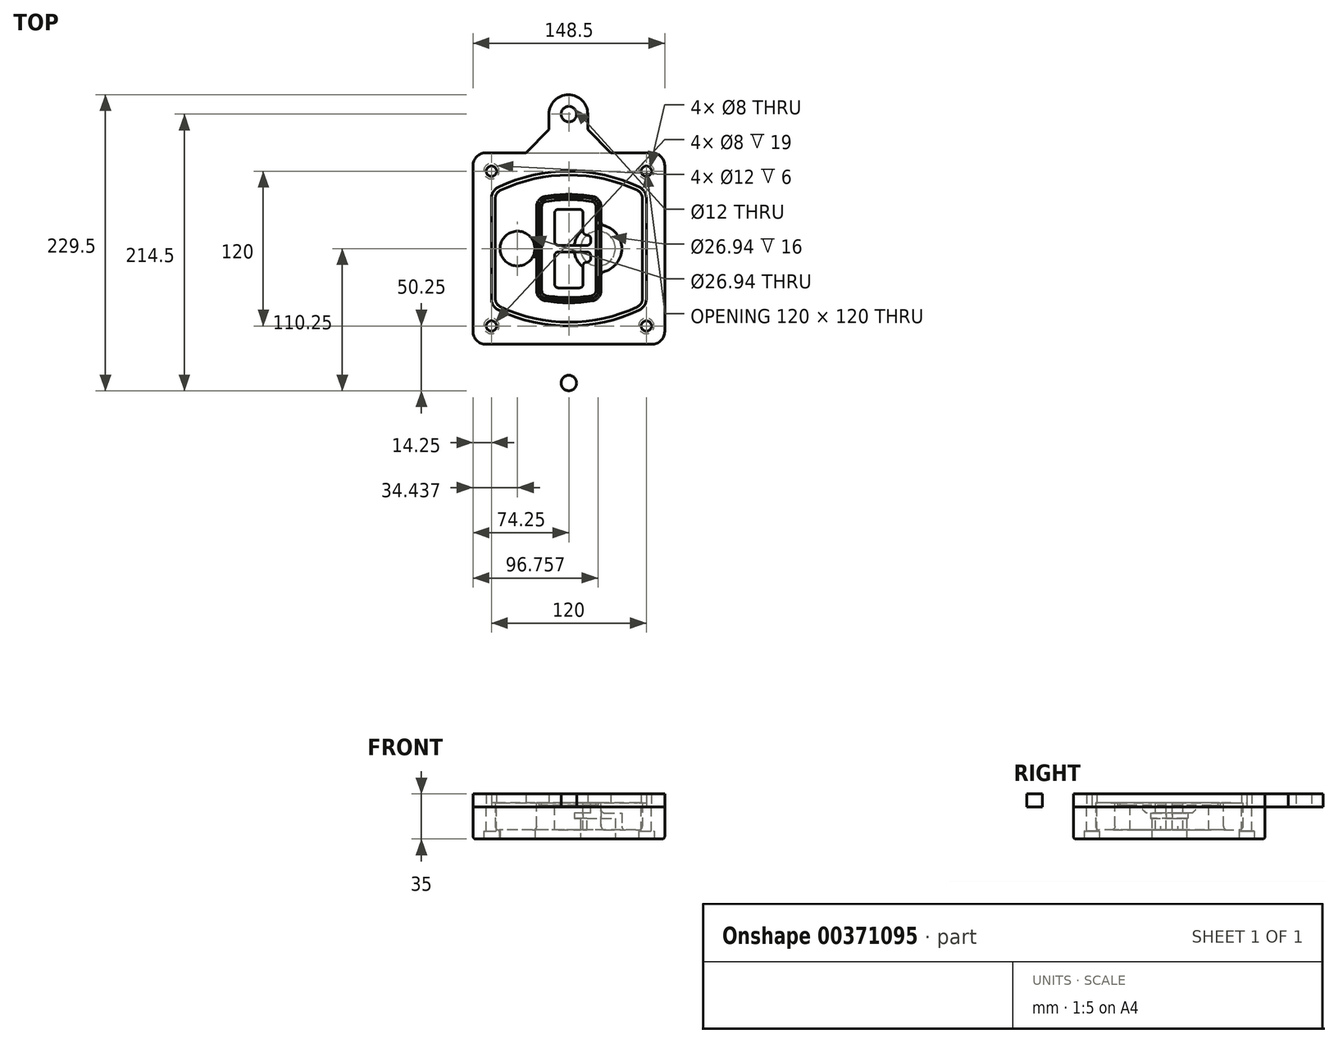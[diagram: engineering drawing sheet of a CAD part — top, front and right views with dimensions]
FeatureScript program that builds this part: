
annotation { "Feature Type Name" : "Feature", "Feature Type Description" : "" }
export const myFeature = defineFeature(function(context is Context, id is Id, definition is map)
    precondition{}
    {
        {
            var Q0;
            Q0=qCreatedBy(makeId("Top.planeOp"),FACE);
            var sketch = newSketch(context, id + "F0", { "sketchPlane" : qUnion([Q0])});
            skPoint(sketch, "E0.rect.middle", {"position": v(0, 0) * mm});
            skLineSegment(sketch, "E1.bottom", {"start": v(-64.25, -74.25) * mm, "end": v(64.25, -74.25) * mm});
            skLineSegment(sketch, "E1.top", {"start": v(-64.25, 74.25) * mm, "end": v(64.25, 74.25) * mm});
            skLineSegment(sketch, "E1.left", {"start": v(-74.25, -64.25) * mm, "end": v(-74.25, 64.25) * mm});
            skLineSegment(sketch, "E1.right", {"start": v(74.25, -64.25) * mm, "end": v(74.25, 64.25) * mm});
            skLineSegment(sketch, "E2", {"start": v(-74.25, 74.25) * mm, "end": v(74.25, -74.25) * mm, "construction": true});
            skLineSegment(sketch, "E3", {"start": v(74.25, 74.25) * mm, "end": v(-74.25, -74.25) * mm, "construction": true});
            skCircle(sketch, "E4", {"center": v(-60, 60) * mm, "radius": 4 * mm});
            skCircle(sketch, "E5", {"center": v(60, 60) * mm, "radius": 4 * mm});
            skCircle(sketch, "E6", {"center": v(60, -60) * mm, "radius": 4 * mm});
            skCircle(sketch, "E7", {"center": v(-60, -60) * mm, "radius": 4 * mm});
            skLineSegment(sketch, "E8", {"start": v(-60, 60) * mm, "end": v(60, 60) * mm, "construction": true});
            skLineSegment(sketch, "E9", {"start": v(60, 60) * mm, "end": v(60, -60) * mm, "construction": true});
            skLineSegment(sketch, "E10", {"start": v(60, -60) * mm, "end": v(-60, -60) * mm, "construction": true});
            skLineSegment(sketch, "E11", {"start": v(-60, -60) * mm, "end": v(-60, 60) * mm, "construction": true});
            skLineSegment(sketch, "E12", {"start": v(-60, 38.83) * mm, "end": v(-60, -38.83) * mm});
            skLineSegment(sketch, "E13", {"start": v(60, 38.83) * mm, "end": v(60, -38.83) * mm});
            skArc(sketch, "E14", {"start": v(54.26, 47.88) * mm, "mid": v(0, 60) * mm, "end": v(-54.26, 47.88) * mm});
            skArc(sketch, "E15", {"start": v(-54.26, -47.88) * mm, "mid": v(0, -60) * mm, "end": v(54.26, -47.88) * mm});
            skLineSegment(sketch, "E16", {"start": v(-60, 0) * mm, "end": v(60, 0) * mm, "construction": true});
            skPoint(sketch, "E17.visualSharp", {"position": v(-60, -45) * mm});
            skArc(sketch, "E17.filletArc", {"start": v(-60, -38.83) * mm, "mid": v(-58.44, -44.2) * mm, "end": v(-54.26, -47.88) * mm});
            skPoint(sketch, "E18.visualSharp", {"position": v(-60, 45) * mm});
            skArc(sketch, "E18.filletArc", {"start": v(-54.26, 47.88) * mm, "mid": v(-58.44, 44.2) * mm, "end": v(-60, 38.83) * mm});
            skPoint(sketch, "E19.visualSharp", {"position": v(60, 45) * mm});
            skArc(sketch, "E19.filletArc", {"start": v(60, 38.83) * mm, "mid": v(58.44, 44.2) * mm, "end": v(54.26, 47.88) * mm});
            skPoint(sketch, "E20.visualSharp", {"position": v(60, -45) * mm});
            skArc(sketch, "E20.filletArc", {"start": v(54.26, -47.88) * mm, "mid": v(58.44, -44.2) * mm, "end": v(60, -38.83) * mm});
            skPoint(sketch, "E21.visualSharp", {"position": v(-74.25, 74.25) * mm});
            skArc(sketch, "E21.filletArc", {"start": v(-64.25, 74.25) * mm, "mid": v(-71.32, 71.32) * mm, "end": v(-74.25, 64.25) * mm});
            skPoint(sketch, "E22.visualSharp", {"position": v(74.25, 74.25) * mm});
            skArc(sketch, "E22.filletArc", {"start": v(74.25, 64.25) * mm, "mid": v(71.32, 71.32) * mm, "end": v(64.25, 74.25) * mm});
            skPoint(sketch, "E23.visualSharp", {"position": v(74.25, -74.25) * mm});
            skArc(sketch, "E23.filletArc", {"start": v(64.25, -74.25) * mm, "mid": v(71.32, -71.32) * mm, "end": v(74.25, -64.25) * mm});
            skPoint(sketch, "E24.visualSharp", {"position": v(-74.25, -74.25) * mm});
            skArc(sketch, "E24.filletArc", {"start": v(-74.25, -64.25) * mm, "mid": v(-71.32, -71.32) * mm, "end": v(-64.25, -74.25) * mm});
            skArc(sketch, "E25.0", {"start": v(57, 38.83) * mm, "mid": v(55.9, 42.58) * mm, "end": v(52.98, 45.17) * mm});
            skLineSegment(sketch, "E25.1", {"start": v(57, 38.83) * mm, "end": v(57, -38.83) * mm});
            skArc(sketch, "E25.2", {"start": v(52.98, -45.17) * mm, "mid": v(55.9, -42.58) * mm, "end": v(57, -38.83) * mm});
            skArc(sketch, "E25.3", {"start": v(-52.98, -45.17) * mm, "mid": v(0, -57) * mm, "end": v(52.98, -45.17) * mm});
            skArc(sketch, "E25.4", {"start": v(-57, -38.83) * mm, "mid": v(-55.9, -42.58) * mm, "end": v(-52.98, -45.17) * mm});
            skArc(sketch, "E25.5", {"start": v(52.98, 45.17) * mm, "mid": v(0, 57) * mm, "end": v(-52.98, 45.17) * mm});
            skLineSegment(sketch, "E25.6", {"start": v(-57, 38.83) * mm, "end": v(-57, -38.83) * mm});
            skArc(sketch, "E25.7", {"start": v(-52.98, 45.17) * mm, "mid": v(-55.9, 42.58) * mm, "end": v(-57, 38.83) * mm});
            skArc(sketch, "E26.0", {"start": v(-55.96, 51.5) * mm, "mid": v(-61.82, 46.33) * mm, "end": v(-64, 38.83) * mm});
            skArc(sketch, "E26.1", {"start": v(55.96, 51.5) * mm, "mid": v(0, 64) * mm, "end": v(-55.96, 51.5) * mm});
            skArc(sketch, "E26.2", {"start": v(64, 38.83) * mm, "mid": v(61.82, 46.33) * mm, "end": v(55.96, 51.5) * mm});
            skLineSegment(sketch, "E26.3", {"start": v(64, 38.83) * mm, "end": v(64, -38.83) * mm});
            skArc(sketch, "E26.4", {"start": v(55.96, -51.5) * mm, "mid": v(61.82, -46.33) * mm, "end": v(64, -38.83) * mm});
            skLineSegment(sketch, "E26.5", {"start": v(-64, 38.83) * mm, "end": v(-64, -38.83) * mm});
            skArc(sketch, "E26.6", {"start": v(-55.96, -51.5) * mm, "mid": v(0, -64) * mm, "end": v(55.96, -51.5) * mm});
            skArc(sketch, "E26.7", {"start": v(-64, -38.83) * mm, "mid": v(-61.82, -46.33) * mm, "end": v(-55.96, -51.5) * mm});
            skSolve(sketch);
        }
        {
            var Q0;
            Q0=makeQuery(id+"F0.imprint","IMPRINT",FACE,{"disambiguationData":[TD([[makeQuery(id+"F0.imprint","IMPRINT",EDGE,{"derivedFrom":sQuery(id+"F0.wireOp",EDGE,"E1.bottom")}),1.0]])]});
            var Q1;
            Q1=makeQuery(id+"F0.imprint","IMPRINT",FACE,{"disambiguationData":[TD([[makeQuery(id+"F0.imprint","IMPRINT",EDGE,{"derivedFrom":sQuery(id+"F0.wireOp",EDGE,"E12")}),1.0]])]});
            var Q2;
            Q2=makeQuery(id+"F0.imprint","IMPRINT",FACE,{"disambiguationData":[TD([[makeQuery(id+"F0.imprint","IMPRINT",EDGE,{"derivedFrom":sQuery(id+"F0.wireOp",EDGE,"E25.0")}),1.0]])]});
            var Q3;
            Q3=makeQuery(id+"F0.imprint","IMPRINT",FACE,{"disambiguationData":[TD([[makeQuery(id+"F0.imprint","IMPRINT",EDGE,{"derivedFrom":sQuery(id+"F0.wireOp",EDGE,"E12")}),-1.0]])]});
            extrude(context, id + "F1", {"entities" : qUnion([Q0, Q1, Q2, Q3]), "oppositeDirection" : true, "depth" : 25 * mm});
        }
        {
            var Q0;
            Q0=makeQuery(id+"F0.imprint","IMPRINT",FACE,{"disambiguationData":[TD([[makeQuery(id+"F0.imprint","IMPRINT",EDGE,{"derivedFrom":sQuery(id+"F0.wireOp",EDGE,"E12")}),1.0]])]});
            extrude(context, id + "F2", {"entities" : qUnion([Q0]), "operationType" : NewBodyOperationType.ADD, "depth" : 3 * mm});
        }
        {
            var Q0;
            Q0=makeQuery(id+"F0.imprint","IMPRINT",FACE,{"disambiguationData":[TD([[makeQuery(id+"F0.imprint","IMPRINT",EDGE,{"derivedFrom":sQuery(id+"F0.wireOp",EDGE,"E25.0")}),1.0]])]});
            extrude(context, id + "F3", {"entities" : qUnion([Q0]), "operationType" : NewBodyOperationType.REMOVE, "oppositeDirection" : true, "depth" : 18 * mm});
        }
        {
            var Q0;
            Q0=makeQuery(id+"F2.opExtrude","CAP_FACE",FACE,{"disambiguationData":[OSD([sQuery(id+"F0.wireOp",EDGE,"E12"),sQuery(id+"F0.wireOp",EDGE,"E13"),sQuery(id+"F0.wireOp",EDGE,"E14"),sQuery(id+"F0.wireOp",EDGE,"E15"),sQuery(id+"F0.wireOp",EDGE,"E17.filletArc"),sQuery(id+"F0.wireOp",EDGE,"E18.filletArc"),sQuery(id+"F0.wireOp",EDGE,"E19.filletArc"),sQuery(id+"F0.wireOp",EDGE,"E20.filletArc"),sQuery(id+"F0.wireOp",EDGE,"E25.0"),sQuery(id+"F0.wireOp",EDGE,"E25.1"),sQuery(id+"F0.wireOp",EDGE,"E25.2"),sQuery(id+"F0.wireOp",EDGE,"E25.3"),sQuery(id+"F0.wireOp",EDGE,"E25.4"),sQuery(id+"F0.wireOp",EDGE,"E25.5"),sQuery(id+"F0.wireOp",EDGE,"E25.6"),sQuery(id+"F0.wireOp",EDGE,"E25.7")])],"isStart":false});
            var sketch = newSketch(context, id + "F4", { "sketchPlane" : qUnion([Q0])});
            skArc(sketch, "E27.0", {"start": v(-18.34, -40.45) * mm, "mid": v(0, -42) * mm, "end": v(18.34, -40.45) * mm});
            skArc(sketch, "E28.0", {"start": v(18.34, 40.45) * mm, "mid": v(0, 42) * mm, "end": v(-18.34, 40.45) * mm});
            skLineSegment(sketch, "E29", {"start": v(-25, 32.57) * mm, "end": v(-25, -32.57) * mm});
            skLineSegment(sketch, "E30", {"start": v(25, 32.57) * mm, "end": v(25, -32.57) * mm});
            skLineSegment(sketch, "E31", {"start": v(-25, 39.1) * mm, "end": v(25, 39.1) * mm, "construction": true});
            skLineSegment(sketch, "E32", {"start": v(-25, -39.1) * mm, "end": v(25, -39.1) * mm, "construction": true});
            skPoint(sketch, "E33.visualSharp", {"position": v(-25, 39.1) * mm});
            skArc(sketch, "E33.filletArc", {"start": v(-18.34, 40.45) * mm, "mid": v(-23.11, 37.73) * mm, "end": v(-25, 32.57) * mm});
            skPoint(sketch, "E34.visualSharp", {"position": v(25, 39.1) * mm});
            skArc(sketch, "E34.filletArc", {"start": v(25, 32.57) * mm, "mid": v(23.11, 37.73) * mm, "end": v(18.34, 40.45) * mm});
            skPoint(sketch, "E35.visualSharp", {"position": v(25, -39.1) * mm});
            skArc(sketch, "E35.filletArc", {"start": v(18.34, -40.45) * mm, "mid": v(23.11, -37.73) * mm, "end": v(25, -32.57) * mm});
            skPoint(sketch, "E36.visualSharp", {"position": v(-25, -39.1) * mm});
            skArc(sketch, "E36.filletArc", {"start": v(-25, -32.57) * mm, "mid": v(-23.11, -37.73) * mm, "end": v(-18.34, -40.45) * mm});
            skArc(sketch, "E37.0", {"start": v(52.98, 45.17) * mm, "mid": v(0, 57) * mm, "end": v(-52.98, 45.17) * mm});
            skArc(sketch, "E37.1", {"start": v(-52.98, 45.17) * mm, "mid": v(-55.9, 42.58) * mm, "end": v(-57, 38.83) * mm});
            skLineSegment(sketch, "E37.2", {"start": v(-57, 38.83) * mm, "end": v(-57, -38.83) * mm});
            skArc(sketch, "E37.3", {"start": v(-57, -38.83) * mm, "mid": v(-55.9, -42.58) * mm, "end": v(-52.98, -45.17) * mm});
            skArc(sketch, "E37.4", {"start": v(-52.98, -45.17) * mm, "mid": v(0, -57) * mm, "end": v(52.98, -45.17) * mm});
            skArc(sketch, "E37.5", {"start": v(52.98, -45.17) * mm, "mid": v(55.9, -42.58) * mm, "end": v(57, -38.83) * mm});
            skLineSegment(sketch, "E37.6", {"start": v(57, 38.83) * mm, "end": v(57, -38.83) * mm});
            skArc(sketch, "E37.7", {"start": v(57, 38.83) * mm, "mid": v(55.9, 42.58) * mm, "end": v(52.98, 45.17) * mm});
            skLineSegment(sketch, "E38.0", {"start": v(23, 32.57) * mm, "end": v(23, -32.57) * mm});
            skArc(sketch, "E38.1", {"start": v(18, -38.48) * mm, "mid": v(21.58, -36.44) * mm, "end": v(23, -32.57) * mm});
            skArc(sketch, "E38.2", {"start": v(-18, -38.48) * mm, "mid": v(0, -40) * mm, "end": v(18, -38.48) * mm});
            skArc(sketch, "E38.3", {"start": v(-23, -32.57) * mm, "mid": v(-21.58, -36.44) * mm, "end": v(-18, -38.48) * mm});
            skLineSegment(sketch, "E38.4", {"start": v(-23, 32.57) * mm, "end": v(-23, -32.57) * mm});
            skArc(sketch, "E38.5", {"start": v(23, 32.57) * mm, "mid": v(21.58, 36.44) * mm, "end": v(18, 38.48) * mm});
            skArc(sketch, "E38.6", {"start": v(-18, 38.48) * mm, "mid": v(-21.58, 36.44) * mm, "end": v(-23, 32.57) * mm});
            skArc(sketch, "E38.7", {"start": v(18, 38.48) * mm, "mid": v(0, 40) * mm, "end": v(-18, 38.48) * mm});
            skArc(sketch, "E39.0", {"start": v(21, 32.57) * mm, "mid": v(20.06, 35.15) * mm, "end": v(17.67, 36.5) * mm});
            skLineSegment(sketch, "E39.1", {"start": v(21, 32.57) * mm, "end": v(21, -32.57) * mm});
            skArc(sketch, "E39.2", {"start": v(17.67, -36.5) * mm, "mid": v(20.06, -35.15) * mm, "end": v(21, -32.57) * mm});
            skArc(sketch, "E39.3", {"start": v(-17.67, -36.5) * mm, "mid": v(0, -38) * mm, "end": v(17.67, -36.5) * mm});
            skArc(sketch, "E39.4", {"start": v(-21, -32.57) * mm, "mid": v(-20.06, -35.15) * mm, "end": v(-17.67, -36.5) * mm});
            skArc(sketch, "E39.5", {"start": v(17.67, 36.5) * mm, "mid": v(0, 38) * mm, "end": v(-17.67, 36.5) * mm});
            skLineSegment(sketch, "E39.6", {"start": v(-21, 32.57) * mm, "end": v(-21, -32.57) * mm});
            skArc(sketch, "E39.7", {"start": v(-17.67, 36.5) * mm, "mid": v(-20.06, 35.15) * mm, "end": v(-21, 32.57) * mm});
            skLineSegment(sketch, "E40", {"start": v(-25, 0) * mm, "end": v(25, 0) * mm, "construction": true});
            skLineSegment(sketch, "E41", {"start": v(-11, 5.5) * mm, "end": v(-11, 27.5) * mm});
            skLineSegment(sketch, "E42", {"start": v(-8, 30.5) * mm, "end": v(8, 30.5) * mm});
            skLineSegment(sketch, "E43", {"start": v(11, 27.5) * mm, "end": v(11, 13.5) * mm});
            skLineSegment(sketch, "E44", {"start": v(14, 10.5) * mm, "end": v(14, 10.5) * mm});
            skLineSegment(sketch, "E45", {"start": v(17, 7.5) * mm, "end": v(17, 5.5) * mm});
            skLineSegment(sketch, "E46", {"start": v(14, 2.5) * mm, "end": v(-8, 2.5) * mm});
            skPoint(sketch, "E47.visualSharp", {"position": v(-11, 30.5) * mm});
            skArc(sketch, "E47.filletArc", {"start": v(-8, 30.5) * mm, "mid": v(-10.12, 29.62) * mm, "end": v(-11, 27.5) * mm});
            skPoint(sketch, "E48.visualSharp", {"position": v(11, 30.5) * mm});
            skArc(sketch, "E48.filletArc", {"start": v(11, 27.5) * mm, "mid": v(10.12, 29.62) * mm, "end": v(8, 30.5) * mm});
            skPoint(sketch, "E49.visualSharp", {"position": v(11, 10.5) * mm});
            skArc(sketch, "E49.filletArc", {"start": v(11, 13.5) * mm, "mid": v(11.88, 11.38) * mm, "end": v(14, 10.5) * mm});
            skPoint(sketch, "E50.visualSharp", {"position": v(17, 10.5) * mm});
            skArc(sketch, "E50.filletArc", {"start": v(17, 7.5) * mm, "mid": v(16.12, 9.62) * mm, "end": v(14, 10.5) * mm});
            skPoint(sketch, "E51.visualSharp", {"position": v(17, 2.5) * mm});
            skArc(sketch, "E51.filletArc", {"start": v(14, 2.5) * mm, "mid": v(16.12, 3.38) * mm, "end": v(17, 5.5) * mm});
            skPoint(sketch, "E52.visualSharp", {"position": v(-11, 2.5) * mm});
            skArc(sketch, "E52.filletArc", {"start": v(-11, 5.5) * mm, "mid": v(-10.12, 3.38) * mm, "end": v(-8, 2.5) * mm});
            skLineSegment(sketch, "E53.0.MirrorCS", {"start": v(14, -2.5) * mm, "end": v(-8, -2.5) * mm});
            skArc(sketch, "E54.0.MirrorCS", {"start": v(-11, -5.5) * mm, "mid": v(-10.12, -3.38) * mm, "end": v(-8, -2.5) * mm});
            skLineSegment(sketch, "E55.0.MirrorCS", {"start": v(-11, -5.5) * mm, "end": v(-11, -27.5) * mm});
            skArc(sketch, "E56.0.MirrorCS", {"start": v(-8, -30.5) * mm, "mid": v(-10.12, -29.62) * mm, "end": v(-11, -27.5) * mm});
            skLineSegment(sketch, "E57.0.MirrorCS", {"start": v(-8, -30.5) * mm, "end": v(8, -30.5) * mm});
            skArc(sketch, "E58.0.MirrorCS", {"start": v(11, -27.5) * mm, "mid": v(10.12, -29.62) * mm, "end": v(8, -30.5) * mm});
            skLineSegment(sketch, "E59.0.MirrorCS", {"start": v(11, -27.5) * mm, "end": v(11, -13.5) * mm});
            skArc(sketch, "E60.0.MirrorCS", {"start": v(11, -13.5) * mm, "mid": v(11.88, -11.38) * mm, "end": v(14, -10.5) * mm});
            skArc(sketch, "E61.0.MirrorCS", {"start": v(17, -7.5) * mm, "mid": v(16.12, -9.62) * mm, "end": v(14, -10.5) * mm});
            skLineSegment(sketch, "E62.0.MirrorCS", {"start": v(17, -7.5) * mm, "end": v(17, -5.5) * mm});
            skArc(sketch, "E63.0.MirrorCS", {"start": v(14, -2.5) * mm, "mid": v(16.12, -3.38) * mm, "end": v(17, -5.5) * mm});
            skSolve(sketch);
        }
        {
            var Q0;
            Q0=makeQuery(id+"F4.imprint","IMPRINT",FACE,{"disambiguationData":[TD([[makeQuery(id+"F4.imprint","IMPRINT",EDGE,{"derivedFrom":sQuery(id+"F4.wireOp",EDGE,"E27.0")}),1.0]])]});
            var Q1;
            Q1=makeQuery(id+"F4.imprint","IMPRINT",FACE,{"disambiguationData":[TD([[makeQuery(id+"F4.imprint","IMPRINT",EDGE,{"derivedFrom":sQuery(id+"F4.wireOp",EDGE,"E38.0")}),-1.0]])]});
            var Q2;
            Q2=makeQuery(id+"F4.imprint","IMPRINT",FACE,{"disambiguationData":[TD([[makeQuery(id+"F4.imprint","IMPRINT",EDGE,{"derivedFrom":sQuery(id+"F4.wireOp",EDGE,"E39.0")}),1.0]])]});
            extrude(context, id + "F5", {"entities" : qUnion([Q0, Q1, Q2]), "operationType" : NewBodyOperationType.ADD, "endBound" : BoundingType.UP_TO_NEXT, "oppositeDirection" : true, "depth" : 25 * mm});
        }
        {
            var Q0;
            Q0=makeQuery(id+"F4.imprint","IMPRINT",FACE,{"disambiguationData":[TD([[makeQuery(id+"F4.imprint","IMPRINT",EDGE,{"derivedFrom":sQuery(id+"F4.wireOp",EDGE,"E38.0")}),-1.0]])]});
            extrude(context, id + "F6", {"entities" : qUnion([Q0]), "operationType" : NewBodyOperationType.REMOVE, "oppositeDirection" : true, "depth" : 2 * mm});
        }
        {
            var Q0;
            Q0=makeQuery(id+"F1.opExtrude","CAP_FACE",FACE,{"disambiguationData":[OSD([sQuery(id+"F0.wireOp",EDGE,"E1.bottom"),sQuery(id+"F0.wireOp",EDGE,"E1.top"),sQuery(id+"F0.wireOp",EDGE,"E1.left"),sQuery(id+"F0.wireOp",EDGE,"E1.right"),sQuery(id+"F0.wireOp",EDGE,"E4"),sQuery(id+"F0.wireOp",EDGE,"E5"),sQuery(id+"F0.wireOp",EDGE,"E6"),sQuery(id+"F0.wireOp",EDGE,"E7"),sQuery(id+"F0.wireOp",EDGE,"E21.filletArc"),sQuery(id+"F0.wireOp",EDGE,"E22.filletArc"),sQuery(id+"F0.wireOp",EDGE,"E23.filletArc"),sQuery(id+"F0.wireOp",EDGE,"E24.filletArc")])],"isStart":false});
            var sketch = newSketch(context, id + "F7", { "sketchPlane" : qUnion([Q0])});
            skCircle(sketch, "E64", {"center": v(22.5, 0) * mm, "radius": 13.47 * mm});
            skCircle(sketch, "E65", {"center": v(-39.81, 0) * mm, "radius": 13.47 * mm});
            skLineSegment(sketch, "E66", {"start": v(74.25, 0) * mm, "end": v(-74.25, 0) * mm});
            skCircle(sketch, "E67", {"center": v(22.5, 0) * mm, "radius": 18.47 * mm});
            skCircle(sketch, "E68", {"center": v(60, -60) * mm, "radius": 6 * mm});
            skCircle(sketch, "E69", {"center": v(-60, -60) * mm, "radius": 6 * mm});
            skCircle(sketch, "E70", {"center": v(-60, 60) * mm, "radius": 6 * mm});
            skCircle(sketch, "E71", {"center": v(60, 60) * mm, "radius": 6 * mm});
            skSolve(sketch);
        }
        {
            var Q0;
            {var subQ1=sQuery(id+"F7.wireOp",EDGE,"E66");var subQ4=sQuery(id+"F7.wireOp",EDGE,"E64");var subQ6=makeQuery(id+"F7.imprint","INTERSECT",VERTEX,{"disambiguationData":[OD(0.0)],"derivedFrom":[subQ4,subQ1]});Q0=makeQuery(id+"F7.imprint","IMPRINT",FACE,{"disambiguationData":[TD([[makeQuery(id+"F7.imprint","IMPRINT",EDGE,{"disambiguationData":[TD([[subQ6,-1.0]])],"derivedFrom":subQ4}),-1.0]])]});}
            var Q1;
            {var subQ0=sQuery(id+"F7.wireOp",EDGE,"E66");var subQ1=sQuery(id+"F7.wireOp",EDGE,"E64");var subQ3=makeQuery(id+"F7.imprint","INTERSECT",VERTEX,{"disambiguationData":[OD(0.0)],"derivedFrom":[subQ1,subQ0]});Q1=makeQuery(id+"F7.imprint","IMPRINT",FACE,{"disambiguationData":[TD([[makeQuery(id+"F7.imprint","IMPRINT",EDGE,{"disambiguationData":[TD([[subQ3,-1.0]])],"derivedFrom":subQ1}),1.0]])]});}
            var Q2;
            {var subQ0=sQuery(id+"F7.wireOp",EDGE,"E66");var subQ1=sQuery(id+"F7.wireOp",EDGE,"E64");var subQ3=makeQuery(id+"F7.imprint","INTERSECT",VERTEX,{"disambiguationData":[OD(0.0)],"derivedFrom":[subQ1,subQ0]});Q2=makeQuery(id+"F7.imprint","IMPRINT",FACE,{"disambiguationData":[TD([[makeQuery(id+"F7.imprint","IMPRINT",EDGE,{"disambiguationData":[TD([[subQ3,1.0]])],"derivedFrom":subQ1}),1.0]])]});}
            var Q3;
            {var subQ1=sQuery(id+"F7.wireOp",EDGE,"E66");var subQ4=sQuery(id+"F7.wireOp",EDGE,"E64");var subQ6=makeQuery(id+"F7.imprint","INTERSECT",VERTEX,{"disambiguationData":[OD(0.0)],"derivedFrom":[subQ4,subQ1]});Q3=makeQuery(id+"F7.imprint","IMPRINT",FACE,{"disambiguationData":[TD([[makeQuery(id+"F7.imprint","IMPRINT",EDGE,{"disambiguationData":[TD([[subQ6,1.0]])],"derivedFrom":subQ4}),-1.0]])]});}
            extrude(context, id + "F8", {"entities" : qUnion([Q0, Q1, Q2, Q3]), "operationType" : NewBodyOperationType.ADD, "oppositeDirection" : true, "depth" : 20 * mm});
        }
        {
            var Q0;
            {var subQ0=sQuery(id+"F7.wireOp",EDGE,"E66");var subQ1=sQuery(id+"F7.wireOp",EDGE,"E64");var subQ3=makeQuery(id+"F7.imprint","INTERSECT",VERTEX,{"disambiguationData":[OD(0.0)],"derivedFrom":[subQ1,subQ0]});Q0=makeQuery(id+"F7.imprint","IMPRINT",FACE,{"disambiguationData":[TD([[makeQuery(id+"F7.imprint","IMPRINT",EDGE,{"disambiguationData":[TD([[subQ3,-1.0]])],"derivedFrom":subQ1}),1.0]])]});}
            var Q1;
            {var subQ0=sQuery(id+"F7.wireOp",EDGE,"E66");var subQ1=sQuery(id+"F7.wireOp",EDGE,"E64");var subQ3=makeQuery(id+"F7.imprint","INTERSECT",VERTEX,{"disambiguationData":[OD(0.0)],"derivedFrom":[subQ1,subQ0]});Q1=makeQuery(id+"F7.imprint","IMPRINT",FACE,{"disambiguationData":[TD([[makeQuery(id+"F7.imprint","IMPRINT",EDGE,{"disambiguationData":[TD([[subQ3,1.0]])],"derivedFrom":subQ1}),1.0]])]});}
            extrude(context, id + "F9", {"entities" : qUnion([Q0, Q1]), "operationType" : NewBodyOperationType.REMOVE, "oppositeDirection" : true, "depth" : 16 * mm});
        }
        {
            var Q0;
            {var subQ0=sQuery(id+"F7.wireOp",EDGE,"E66");var subQ1=sQuery(id+"F7.wireOp",EDGE,"E65");var subQ3=makeQuery(id+"F7.imprint","INTERSECT",VERTEX,{"disambiguationData":[OD(0.0)],"derivedFrom":[subQ1,subQ0]});Q0=makeQuery(id+"F7.imprint","IMPRINT",FACE,{"disambiguationData":[TD([[makeQuery(id+"F7.imprint","IMPRINT",EDGE,{"disambiguationData":[TD([[subQ3,-1.0]])],"derivedFrom":subQ1}),1.0]])]});}
            var Q1;
            {var subQ0=sQuery(id+"F7.wireOp",EDGE,"E66");var subQ1=sQuery(id+"F7.wireOp",EDGE,"E65");var subQ3=makeQuery(id+"F7.imprint","INTERSECT",VERTEX,{"disambiguationData":[OD(0.0)],"derivedFrom":[subQ1,subQ0]});Q1=makeQuery(id+"F7.imprint","IMPRINT",FACE,{"disambiguationData":[TD([[makeQuery(id+"F7.imprint","IMPRINT",EDGE,{"disambiguationData":[TD([[subQ3,1.0]])],"derivedFrom":subQ1}),1.0]])]});}
            extrude(context, id + "F10", {"entities" : qUnion([Q0, Q1]), "operationType" : NewBodyOperationType.REMOVE, "oppositeDirection" : true, "depth" : 25 * mm});
        }
        {
            var Q0;
            Q0=makeQuery(id+"F7.imprint","IMPRINT",FACE,{"disambiguationData":[TD([[makeQuery(id+"F7.imprint","IMPRINT",EDGE,{"derivedFrom":sQuery(id+"F7.wireOp",EDGE,"E68")}),1.0]])]});
            var Q1;
            Q1=makeQuery(id+"F7.imprint","IMPRINT",FACE,{"disambiguationData":[TD([[makeQuery(id+"F7.imprint","IMPRINT",EDGE,{"derivedFrom":makeQuery(id+"F1.opExtrude","CAP_EDGE",EDGE,{"disambiguationData":[OSD([sQuery(id+"F0.wireOp",EDGE,"E5")])],"isStart":false})}),-1.0]])]});
            var Q2;
            Q2=makeQuery(id+"F7.imprint","IMPRINT",FACE,{"disambiguationData":[TD([[makeQuery(id+"F7.imprint","IMPRINT",EDGE,{"derivedFrom":sQuery(id+"F7.wireOp",EDGE,"E69")}),1.0]])]});
            var Q3;
            Q3=makeQuery(id+"F7.imprint","IMPRINT",FACE,{"disambiguationData":[TD([[makeQuery(id+"F7.imprint","IMPRINT",EDGE,{"derivedFrom":makeQuery(id+"F1.opExtrude","CAP_EDGE",EDGE,{"disambiguationData":[OSD([sQuery(id+"F0.wireOp",EDGE,"E4")])],"isStart":false})}),-1.0]])]});
            var Q4;
            Q4=makeQuery(id+"F7.imprint","IMPRINT",FACE,{"disambiguationData":[TD([[makeQuery(id+"F7.imprint","IMPRINT",EDGE,{"derivedFrom":sQuery(id+"F7.wireOp",EDGE,"E70")}),1.0]])]});
            var Q5;
            Q5=makeQuery(id+"F7.imprint","IMPRINT",FACE,{"disambiguationData":[TD([[makeQuery(id+"F7.imprint","IMPRINT",EDGE,{"derivedFrom":makeQuery(id+"F1.opExtrude","CAP_EDGE",EDGE,{"disambiguationData":[OSD([sQuery(id+"F0.wireOp",EDGE,"E7")])],"isStart":false})}),-1.0]])]});
            var Q6;
            Q6=makeQuery(id+"F7.imprint","IMPRINT",FACE,{"disambiguationData":[TD([[makeQuery(id+"F7.imprint","IMPRINT",EDGE,{"derivedFrom":sQuery(id+"F7.wireOp",EDGE,"E71")}),1.0]])]});
            var Q7;
            Q7=makeQuery(id+"F7.imprint","IMPRINT",FACE,{"disambiguationData":[TD([[makeQuery(id+"F7.imprint","IMPRINT",EDGE,{"derivedFrom":makeQuery(id+"F1.opExtrude","CAP_EDGE",EDGE,{"disambiguationData":[OSD([sQuery(id+"F0.wireOp",EDGE,"E6")])],"isStart":false})}),-1.0]])]});
            extrude(context, id + "F11", {"entities" : qUnion([Q0, Q1, Q2, Q3, Q4, Q5, Q6, Q7]), "operationType" : NewBodyOperationType.REMOVE, "oppositeDirection" : true, "depth" : 6 * mm});
        }
        {
            var Q0;
            Q0=makeQuery(id+"F9.boolean.opBoolean","COPY",FACE,{"derivedFrom":makeQuery(id+"F9.opExtrude","CAP_FACE",FACE,{"disambiguationData":[OSD([sQuery(id+"F7.wireOp",EDGE,"E64")])],"isStart":false})});
            var sketch = newSketch(context, id + "F12", { "sketchPlane" : qUnion([Q0])});
            skArc(sketch, "E72.0", {"start": v(11, 14.45) * mm, "mid": v(6.45, 9.13) * mm, "end": v(4.2, 2.5) * mm});
            skArc(sketch, "E72.1", {"start": v(4.2, -2.5) * mm, "mid": v(6.45, -9.13) * mm, "end": v(11, -14.45) * mm});
            skLineSegment(sketch, "E73", {"start": v(4.2, -2.5) * mm, "end": v(14, -2.5) * mm});
            skLineSegment(sketch, "E74.0", {"start": v(14, 2.5) * mm, "end": v(4.2, 2.5) * mm});
            skArc(sketch, "E74.1", {"start": v(14, 2.5) * mm, "mid": v(16.12, 3.38) * mm, "end": v(17, 5.5) * mm});
            skLineSegment(sketch, "E74.2", {"start": v(17, 7.5) * mm, "end": v(17, 5.5) * mm});
            skArc(sketch, "E74.3", {"start": v(17, 7.5) * mm, "mid": v(16.12, 9.62) * mm, "end": v(14, 10.5) * mm});
            skArc(sketch, "E74.4", {"start": v(11, 13.5) * mm, "mid": v(11.88, 11.38) * mm, "end": v(14, 10.5) * mm});
            skLineSegment(sketch, "E74.5", {"start": v(11, 14.45) * mm, "end": v(11, 13.5) * mm});
            skLineSegment(sketch, "E74.7", {"start": v(14, -2.5) * mm, "end": v(4.2, -2.5) * mm});
            skArc(sketch, "E74.8", {"start": v(14, -2.5) * mm, "mid": v(16.12, -3.38) * mm, "end": v(17, -5.5) * mm});
            skLineSegment(sketch, "E74.9", {"start": v(17, -7.5) * mm, "end": v(17, -5.5) * mm});
            skArc(sketch, "E74.10", {"start": v(17, -7.5) * mm, "mid": v(16.12, -9.62) * mm, "end": v(14, -10.5) * mm});
            skArc(sketch, "E74.11", {"start": v(11, -13.5) * mm, "mid": v(11.88, -11.38) * mm, "end": v(14, -10.5) * mm});
            skLineSegment(sketch, "E74.12", {"start": v(11, -14.45) * mm, "end": v(11, -13.5) * mm});
            skPoint(sketch, "E75.orphan", {"position": v(11, -27.5) * mm});
            skPoint(sketch, "E76.orphan", {"position": v(-8, -2.5) * mm});
            skPoint(sketch, "E77.orphan", {"position": v(-8, 2.5) * mm});
            skPoint(sketch, "E78.orphan", {"position": v(11, 27.5) * mm});
            skSolve(sketch);
        }
        {
            var Q0;
            {var subQ7=sQuery(id+"F12.wireOp",EDGE,"E72.0");var subQ14=sQuery(id+"F12.wireOp",EDGE,"E72.1");var subQ16=sQuery(id+"F12.wireOp",EDGE,"E74.1");var subQ18=sQuery(id+"F12.wireOp",EDGE,"E74.8");Q0=qUnion([makeQuery(id+"F12.imprint","IMPRINT",FACE,{"disambiguationData":[TD([[makeQuery(id+"F12.imprint","IMPRINT",EDGE,{"derivedFrom":subQ7}),1.0]])]}),makeQuery(id+"F12.imprint","IMPRINT",FACE,{"disambiguationData":[TD([[makeQuery(id+"F12.imprint","IMPRINT",EDGE,{"derivedFrom":subQ14}),1.0]])]}),makeQuery(id+"F12.imprint","IMPRINT",FACE,{"disambiguationData":[TD([[makeQuery(id+"F12.imprint","IMPRINT",EDGE,{"derivedFrom":subQ16}),1.0]])]}),makeQuery(id+"F12.imprint","IMPRINT",FACE,{"disambiguationData":[TD([[makeQuery(id+"F12.imprint","IMPRINT",EDGE,{"derivedFrom":subQ18}),-1.0]])]})]);}
            var Q1;
            Q1=makeQuery(id+"F5.boolean.opBoolean","SPLIT",FACE,{"disambiguationData":[TD([makeQuery(id+"F5.opExtrude","SWEPT_FACE",FACE,{"disambiguationData":[OSD([sQuery(id+"F4.wireOp",EDGE,"E41")])]})])],"derivedFrom":makeQuery(id+"F3.boolean.opBoolean","COPY",FACE,{"derivedFrom":makeQuery(id+"F3.opExtrude","CAP_FACE",FACE,{"disambiguationData":[OSD([sQuery(id+"F0.wireOp",EDGE,"E25.0"),sQuery(id+"F0.wireOp",EDGE,"E25.1"),sQuery(id+"F0.wireOp",EDGE,"E25.2"),sQuery(id+"F0.wireOp",EDGE,"E25.3"),sQuery(id+"F0.wireOp",EDGE,"E25.4"),sQuery(id+"F0.wireOp",EDGE,"E25.5"),sQuery(id+"F0.wireOp",EDGE,"E25.6"),sQuery(id+"F0.wireOp",EDGE,"E25.7")])],"isStart":false})})});
            extrude(context, id + "F13", {"entities" : qUnion([Q0]), "operationType" : NewBodyOperationType.REMOVE, "endBound" : BoundingType.UP_TO_SURFACE, "endBoundEntityFace" : qUnion([Q1]), "depth" : 25 * mm});
        }
        {
            var Q0;
            Q0=makeQuery(id+"F3.boolean.opBoolean","COPY",EDGE,{"derivedFrom":makeQuery(id+"F3.opExtrude","CAP_EDGE",EDGE,{"disambiguationData":[OSD([sQuery(id+"F0.wireOp",EDGE,"E25.6")])],"isStart":false})});
            var Q1;
            Q1=makeQuery(id+"F8.boolean.opBoolean","INTERSECT",EDGE,{"derivedFrom":[makeQuery(id+"F5.opExtrude","SWEPT_FACE",FACE,{"disambiguationData":[OSD([sQuery(id+"F4.wireOp",EDGE,"E30")])]}),makeQuery(id+"F8.opExtrude","CAP_FACE",FACE,{"disambiguationData":[OSD([sQuery(id+"F7.wireOp",EDGE,"E67")])],"isStart":false})]});
            var Q2;
            Q2=makeQuery(id+"F8.boolean.opBoolean","INTERSECT",EDGE,{"disambiguationData":[OD(1.0)],"derivedFrom":[makeQuery(id+"F5.opExtrude","SWEPT_FACE",FACE,{"disambiguationData":[OSD([sQuery(id+"F4.wireOp",EDGE,"E30")])]}),makeQuery(id+"F8.opExtrude","SWEPT_FACE",FACE,{"disambiguationData":[OSD([sQuery(id+"F7.wireOp",EDGE,"E67")])]})]});
            var Q3;
            {var subQ0=sQuery(id+"F4.wireOp",EDGE,"E30");Q3=makeQuery(id+"F8.boolean.opBoolean","SPLIT",EDGE,{"disambiguationData":[TD([makeQuery(id+"F5.opExtrude","SWEPT_FACE",FACE,{"disambiguationData":[OSD([sQuery(id+"F4.wireOp",EDGE,"E35.filletArc")])]})])],"derivedFrom":makeQuery(id+"F5.opExtrude","CAP_EDGE",EDGE,{"disambiguationData":[OSD([subQ0])],"isStart":false})});}
            var Q4;
            {var subQ0=sQuery(id+"F0.wireOp",EDGE,"E25.7");var subQ1=sQuery(id+"F0.wireOp",EDGE,"E25.1");var subQ2=sQuery(id+"F0.wireOp",EDGE,"E25.6");var subQ3=sQuery(id+"F0.wireOp",EDGE,"E25.5");var subQ4=sQuery(id+"F0.wireOp",EDGE,"E25.4");var subQ5=sQuery(id+"F0.wireOp",EDGE,"E25.0");var subQ6=sQuery(id+"F0.wireOp",EDGE,"E25.2");var subQ7=sQuery(id+"F0.wireOp",EDGE,"E25.3");Q4=makeQuery(id+"F8.boolean.opBoolean","INTERSECT",EDGE,{"derivedFrom":[makeQuery(id+"F5.boolean.opBoolean","SPLIT",FACE,{"disambiguationData":[TD([makeQuery(id+"F2.opExtrude","SWEPT_FACE",FACE,{"disambiguationData":[OSD([subQ5])]})])],"derivedFrom":makeQuery(id+"F3.boolean.opBoolean","COPY",FACE,{"derivedFrom":makeQuery(id+"F3.opExtrude","CAP_FACE",FACE,{"disambiguationData":[OSD([subQ5,subQ1,subQ6,subQ7,subQ4,subQ3,subQ2,subQ0])],"isStart":false})})}),makeQuery(id+"F8.opExtrude","SWEPT_FACE",FACE,{"disambiguationData":[OSD([sQuery(id+"F7.wireOp",EDGE,"E67")])]})]});}
            var Q5;
            Q5=makeQuery(id+"F8.boolean.opBoolean","INTERSECT",EDGE,{"disambiguationData":[OD(0.0)],"derivedFrom":[makeQuery(id+"F5.opExtrude","SWEPT_FACE",FACE,{"disambiguationData":[OSD([sQuery(id+"F4.wireOp",EDGE,"E30")])]}),makeQuery(id+"F8.opExtrude","SWEPT_FACE",FACE,{"disambiguationData":[OSD([sQuery(id+"F7.wireOp",EDGE,"E67")])]})]});
            fillet(context, id + "F14", {"entities" : qUnion([Q0, Q1, Q2, Q3, Q4, Q5]), "radius" : 3 * mm, "tangentPropagation" : true, "allowEdgeOverflow" : false});
        }
        {
            var Q0;
            Q0=makeQuery(id+"F1.opExtrude","CAP_EDGE",EDGE,{"disambiguationData":[OSD([sQuery(id+"F0.wireOp",EDGE,"E1.bottom")])],"isStart":false});
            fillet(context, id + "F15", {"entities" : qUnion([Q0]), "radius" : 2 * mm, "tangentPropagation" : true, "allowEdgeOverflow" : false});
        }
        {
            var Q0;
            {var subQ0=sQuery(id+"F0.wireOp",EDGE,"E21.filletArc");var subQ1=sQuery(id+"F0.wireOp",EDGE,"E7");var subQ2=sQuery(id+"F0.wireOp",EDGE,"E6");var subQ3=sQuery(id+"F0.wireOp",EDGE,"E5");var subQ4=sQuery(id+"F0.wireOp",EDGE,"E4");var subQ5=sQuery(id+"F0.wireOp",EDGE,"E22.filletArc");var subQ6=sQuery(id+"F0.wireOp",EDGE,"E1.bottom");var subQ7=sQuery(id+"F0.wireOp",EDGE,"E1.right");var subQ8=sQuery(id+"F0.wireOp",EDGE,"E1.top");var subQ9=sQuery(id+"F0.wireOp",EDGE,"E1.left");var subQ10=sQuery(id+"F0.wireOp",EDGE,"E23.filletArc");var subQ11=sQuery(id+"F0.wireOp",EDGE,"E24.filletArc");Q0=makeQuery(id+"F2.boolean.opBoolean","SPLIT",FACE,{"disambiguationData":[TD([makeQuery(id+"F1.opExtrude","SWEPT_FACE",FACE,{"disambiguationData":[OSD([subQ6])]})])],"derivedFrom":makeQuery(id+"F1.opExtrude","CAP_FACE",FACE,{"disambiguationData":[OSD([subQ6,subQ8,subQ9,subQ7,subQ4,subQ3,subQ2,subQ1,subQ0,subQ5,subQ10,subQ11])],"isStart":true})});}
            var sketch = newSketch(context, id + "F16", { "sketchPlane" : qUnion([Q0])});
            skCircle(sketch, "E79", {"center": v(0, 104.25) * mm, "radius": 6 * mm});
            skLineSegment(sketch, "E80", {"start": v(-15.38, 92.25) * mm, "end": v(-33.38, 74.25) * mm});
            skLineSegment(sketch, "E81", {"start": v(-15.38, 92.25) * mm, "end": v(-15.38, 104.25) * mm});
            skArc(sketch, "E82", {"start": v(14.62, 104.25) * mm, "mid": v(-0.38, 119.25) * mm, "end": v(-15.38, 104.25) * mm});
            skLineSegment(sketch, "E83", {"start": v(14.62, 104.25) * mm, "end": v(14.62, 92.25) * mm});
            skLineSegment(sketch, "E84", {"start": v(14.62, 92.25) * mm, "end": v(32.62, 74.25) * mm});
            skPoint(sketch, "E85.startSnap0", {"position": v(74.25, 0) * mm});
            skPoint(sketch, "E85.endSnap0", {"position": v(-74.25, 0) * mm});
            skCircle(sketch, "E86.MirrorC", {"center": v(0, -104.25) * mm, "radius": 6 * mm});
            skLineSegment(sketch, "E87.MirrorCS", {"start": v(-15.38, -92.25) * mm, "end": v(-15.38, -104.25) * mm});
            skArc(sketch, "E88.MirrorCS", {"start": v(14.62, -104.25) * mm, "mid": v(-0.38, -119.25) * mm, "end": v(-15.38, -104.25) * mm});
            skLineSegment(sketch, "E89.MirrorCS", {"start": v(14.62, -104.25) * mm, "end": v(14.62, -92.25) * mm});
            skLineSegment(sketch, "E90.MirrorCS", {"start": v(14.62, -92.25) * mm, "end": v(32.62, -74.25) * mm});
            skLineSegment(sketch, "E91.MirrorCS", {"start": v(-15.38, -92.25) * mm, "end": v(-33.38, -74.25) * mm});
            skSolve(sketch);
        }
        {
            var Q0;
            Q0=makeQuery(id+"F16.imprint","IMPRINT",FACE,{"disambiguationData":[TD([[makeQuery(id+"F16.imprint","IMPRINT",EDGE,{"derivedFrom":sQuery(id+"F16.wireOp",EDGE,"E86.MirrorC")}),1.0]])]});
            var Q1;
            Q1=makeQuery(id+"F16.imprint","IMPRINT",FACE,{"disambiguationData":[TD([[makeQuery(id+"F16.imprint","IMPRINT",EDGE,{"derivedFrom":makeQuery(id+"F1.opExtrude","CAP_EDGE",EDGE,{"disambiguationData":[OSD([sQuery(id+"F0.wireOp",EDGE,"E1.left")])],"isStart":true})}),-1.0]])]});
            var Q2;
            Q2=makeQuery(id+"F16.imprint","IMPRINT",FACE,{"disambiguationData":[TD([[makeQuery(id+"F16.imprint","IMPRINT",EDGE,{"derivedFrom":sQuery(id+"F16.wireOp",EDGE,"E79")}),-1.0]])]});
            extrude(context, id + "F17", {"entities" : qUnion([Q0, Q1, Q2]), "depth" : 10 * mm});
        }
    });
